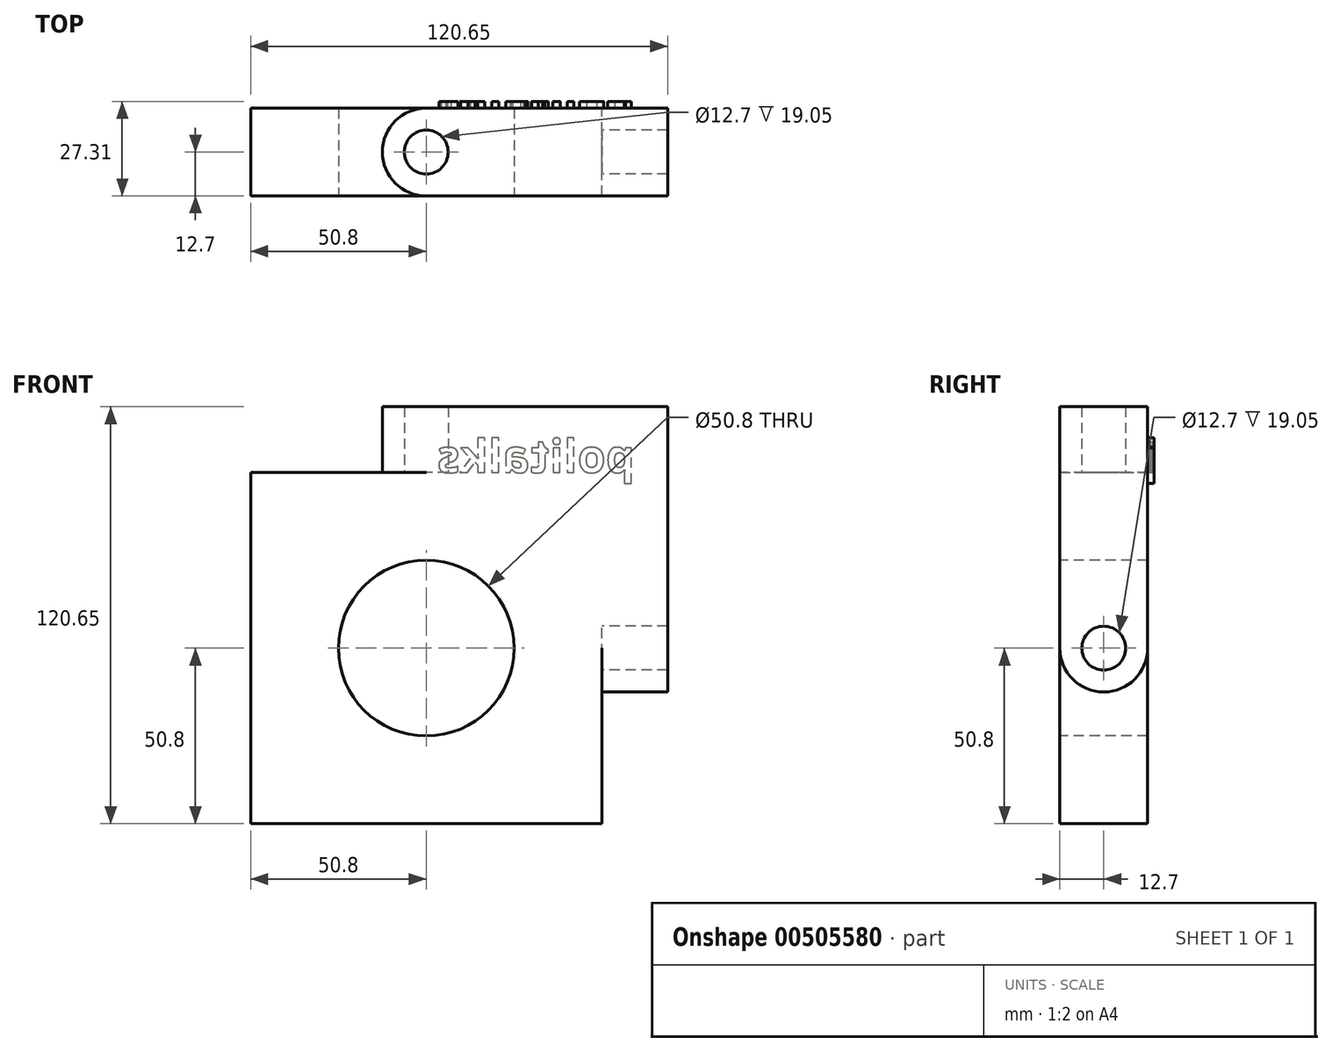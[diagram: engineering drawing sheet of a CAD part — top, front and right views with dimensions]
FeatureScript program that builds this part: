
annotation { "Feature Type Name" : "Feature", "Feature Type Description" : "" }
export const myFeature = defineFeature(function(context is Context, id is Id, definition is map)
    precondition{}
    {
        {
            var Q0;
            Q0=qCreatedBy(makeId("Front.planeOp"),FACE);
            var sketch = newSketch(context, id + "F0", { "sketchPlane" : qUnion([Q0])});
            skLineSegment(sketch, "E0", {"start": v(0, 0) * mm, "end": v(0, 101.6) * mm});
            skLineSegment(sketch, "E1", {"start": v(0, 101.6) * mm, "end": v(101.6, 101.6) * mm});
            skLineSegment(sketch, "E2", {"start": v(101.6, 101.6) * mm, "end": v(101.6, 0) * mm});
            skLineSegment(sketch, "E3", {"start": v(101.6, 0) * mm, "end": v(0, 0) * mm});
            skSolve(sketch);
        }
        {
            var Q0;
            Q0=makeQuery(id+"F0.imprint","IMPRINT",FACE,{"disambiguationData":[TD([[makeQuery(id+"F0.imprint","IMPRINT",EDGE,{"derivedFrom":sQuery(id+"F0.wireOp",EDGE,"E0")}),-1.0]])]});
            extrude(context, id + "F1", {"entities" : qUnion([Q0]), "depth" : 25.4 * mm});
        }
        {
            var Q0;
            Q0=makeQuery(id+"F1.opExtrude","SWEPT_FACE",FACE,{"disambiguationData":[OSD([sQuery(id+"F0.wireOp",EDGE,"E1")])]});
            var sketch = newSketch(context, id + "F2", { "sketchPlane" : qUnion([Q0])});
            skCircle(sketch, "E4", {"center": v(50.8, -12.7) * mm, "radius": 6.35 * mm});
            skArc(sketch, "E5", {"start": v(50.8, 0) * mm, "mid": v(38.1, -12.7) * mm, "end": v(50.8, -25.4) * mm});
            skLineSegment(sketch, "E6", {"start": v(50.8, 0) * mm, "end": v(101.6, 0) * mm});
            skLineSegment(sketch, "E7", {"start": v(101.6, 0) * mm, "end": v(101.6, -25.4) * mm});
            skLineSegment(sketch, "E8", {"start": v(101.6, -25.4) * mm, "end": v(50.8, -25.4) * mm});
            skSolve(sketch);
        }
        {
            var Q0;
            Q0=makeQuery(id+"F2.imprint","IMPRINT",FACE,{"disambiguationData":[TD([[makeQuery(id+"F2.imprint","IMPRINT",EDGE,{"derivedFrom":sQuery(id+"F2.wireOp",EDGE,"E4")}),-1.0]])]});
            extrude(context, id + "F3", {"entities" : qUnion([Q0]), "operationType" : NewBodyOperationType.ADD, "depth" : 19.05 * mm});
        }
        {
            var Q0;
            Q0=makeQuery(id+"F3.boolean.opBoolean","MERGE",FACE,{"derivedFrom":[makeQuery(id+"F1.opExtrude","SWEPT_FACE",FACE,{"disambiguationData":[OSD([sQuery(id+"F0.wireOp",EDGE,"E2")])]}),makeQuery(id+"F3.opExtrude","SWEPT_FACE",FACE,{"disambiguationData":[OSD([sQuery(id+"F2.wireOp",EDGE,"E7")])]})]});
            var sketch = newSketch(context, id + "F4", { "sketchPlane" : qUnion([Q0])});
            skCircle(sketch, "E9", {"center": v(-12.7, 50.8) * mm, "radius": 6.35 * mm});
            skArc(sketch, "E10", {"start": v(-25.4, 50.8) * mm, "mid": v(-12.7, 38.1) * mm, "end": v(0, 50.8) * mm});
            skLineSegment(sketch, "E11", {"start": v(-25.4, 120.65) * mm, "end": v(-25.4, 50.8) * mm});
            skLineSegment(sketch, "E12", {"start": v(-25.4, 120.65) * mm, "end": v(0, 120.65) * mm});
            skLineSegment(sketch, "E13", {"start": v(0, 120.65) * mm, "end": v(0, 50.8) * mm});
            skSolve(sketch);
        }
        {
            var Q0;
            Q0 = qSketchRegion(id + "F4", true);
            extrude(context, id + "F5", {"entities" : qUnion([Q0]), "operationType" : NewBodyOperationType.ADD, "depth" : 19.05 * mm});
        }
        {
            var Q0;
            Q0=makeQuery(id+"F5.boolean.opBoolean","MERGE",FACE,{"derivedFrom":[makeQuery(id+"F3.boolean.opBoolean","MERGE",FACE,{"derivedFrom":[makeQuery(id+"F1.opExtrude","CAP_FACE",FACE,{"disambiguationData":[OSD([sQuery(id+"F0.wireOp",EDGE,"E0"),sQuery(id+"F0.wireOp",EDGE,"E1"),sQuery(id+"F0.wireOp",EDGE,"E2"),sQuery(id+"F0.wireOp",EDGE,"E3")])],"isStart":false}),makeQuery(id+"F3.opExtrude","SWEPT_FACE",FACE,{"disambiguationData":[OSD([sQuery(id+"F2.wireOp",EDGE,"E8")])]})]}),makeQuery(id+"F5.opExtrude","SWEPT_FACE",FACE,{"disambiguationData":[OSD([sQuery(id+"F4.wireOp",EDGE,"E11")])]})]});
            var sketch = newSketch(context, id + "F6", { "sketchPlane" : qUnion([Q0])});
            skLineSegment(sketch, "E14", {"start": v(0, 0) * mm, "end": v(0, 50.8) * mm});
            skCircle(sketch, "E15", {"center": v(50.8, 50.8) * mm, "radius": 25.4 * mm});
            skSolve(sketch);
        }
        {
            var Q0;
            Q0=makeQuery(id+"F6.imprint","IMPRINT",FACE,{"disambiguationData":[TD([[makeQuery(id+"F6.imprint","IMPRINT",EDGE,{"derivedFrom":sQuery(id+"F6.wireOp",EDGE,"E15")}),1.0]])]});
            extrude(context, id + "F7", {"entities" : qUnion([Q0]), "operationType" : NewBodyOperationType.REMOVE, "oppositeDirection" : true, "depth" : 25.4 * mm});
        }
        {
            var Q0;
            Q0=makeQuery(id+"F5.boolean.opBoolean","MERGE",FACE,{"derivedFrom":[makeQuery(id+"F3.boolean.opBoolean","MERGE",FACE,{"derivedFrom":[makeQuery(id+"F1.opExtrude","CAP_FACE",FACE,{"disambiguationData":[OSD([sQuery(id+"F0.wireOp",EDGE,"E0"),sQuery(id+"F0.wireOp",EDGE,"E1"),sQuery(id+"F0.wireOp",EDGE,"E2"),sQuery(id+"F0.wireOp",EDGE,"E3")])],"isStart":true}),makeQuery(id+"F3.opExtrude","SWEPT_FACE",FACE,{"disambiguationData":[OSD([sQuery(id+"F2.wireOp",EDGE,"E6")])]})]}),makeQuery(id+"F5.opExtrude","SWEPT_FACE",FACE,{"disambiguationData":[OSD([sQuery(id+"F4.wireOp",EDGE,"E13")])]})]});
            var sketch = newSketch(context, id + "F8", { "sketchPlane" : qUnion([Q0])});
            skLineSegment(sketch, "E16", {"start": v(-120.65, 120.65) * mm, "end": v(-111.12, 120.65) * mm});
            skLineSegment(sketch, "E17", {"start": v(-111.12, 120.65) * mm, "end": v(-111.12, 111.12) * mm});
            skLineSegment(sketch, "E18", {"start": v(-50.8, 101.6) * mm, "end": v(-53.58, 101.6) * mm});
            skText(sketch, "E19", { "text": "politalks\n", "fontName": "OpenSans-Bold.ttf"});
            const initialGuessF8  = {"E19": [-0.11112, 0.1016, 1, 0, 0.00952]};
            skSetInitialGuess(sketch, initialGuessF8);
            skSolve(sketch);
        }
        {
            var Q0;
            Q0 = qSketchRegion(id + "F8", true);
            extrude(context, id + "F9", {"entities" : qUnion([Q0]), "operationType" : NewBodyOperationType.ADD, "depth" : 1.9 * mm});
        }
    });
